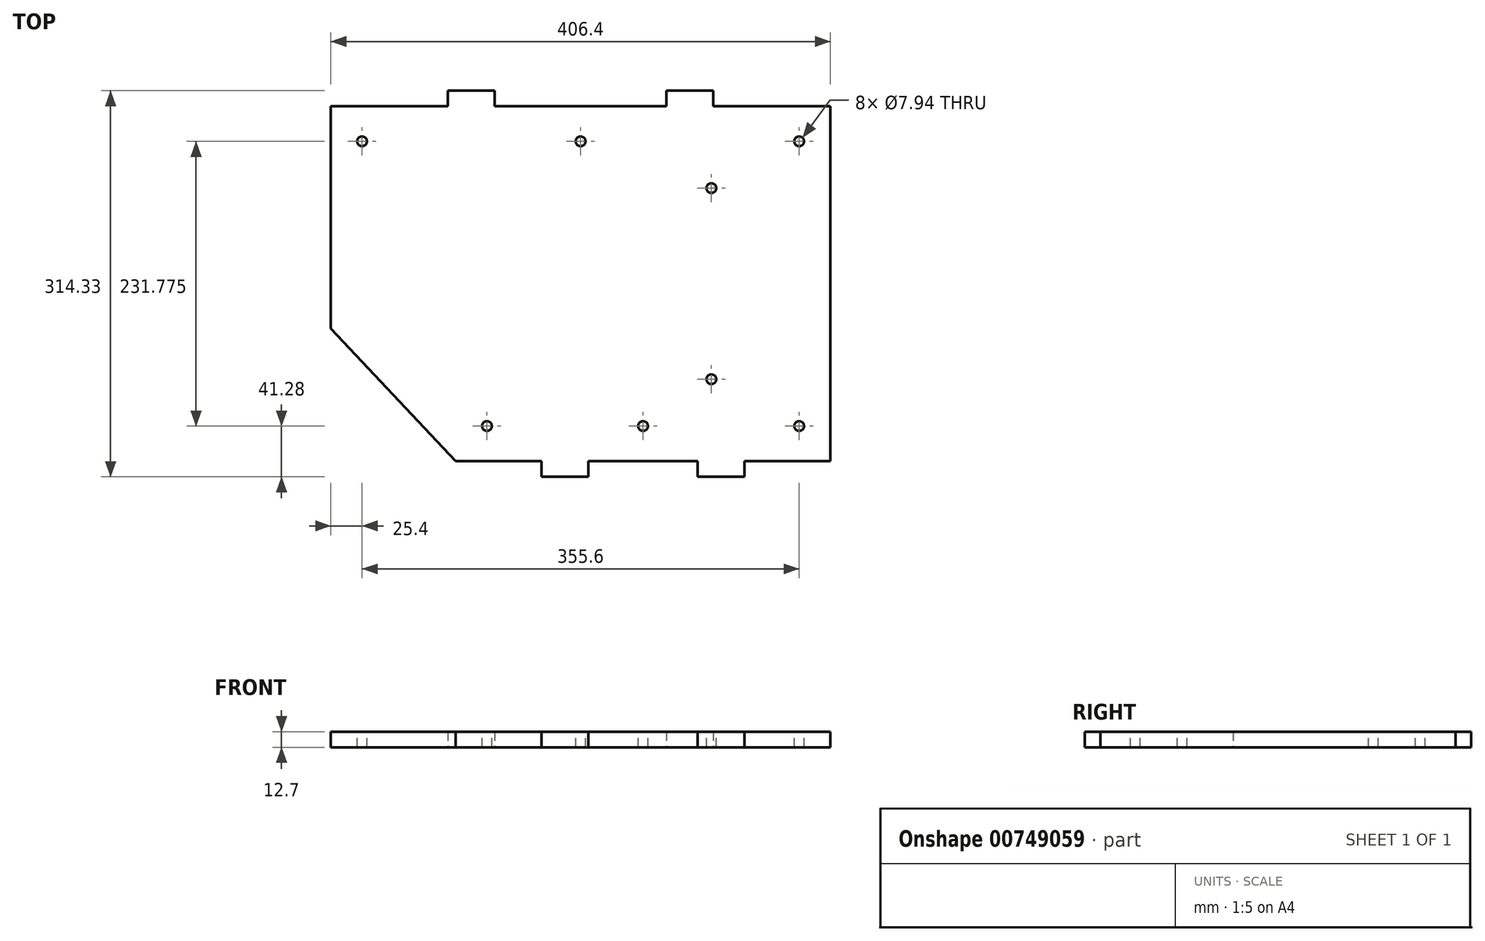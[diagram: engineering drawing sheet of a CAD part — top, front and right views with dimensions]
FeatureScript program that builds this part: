
annotation { "Feature Type Name" : "Feature", "Feature Type Description" : "" }
export const myFeature = defineFeature(function(context is Context, id is Id, definition is map)
    precondition{}
    {
        {
            var Q0;
            Q0=qCreatedBy(makeId("Top.planeOp"),FACE);
            var sketch = newSketch(context, id + "F0", { "sketchPlane" : qUnion([Q0])});
            skLineSegment(sketch, "E0", {"start": v(-127, -25.4) * mm, "end": v(-127, -314.32) * mm});
            skLineSegment(sketch, "E1", {"start": v(-127, -314.32) * mm, "end": v(-196.85, -314.33) * mm});
            skLineSegment(sketch, "E2", {"start": v(-431.8, -314.32) * mm, "end": v(-533.4, -206.38) * mm});
            skLineSegment(sketch, "E3", {"start": v(-533.4, -206.38) * mm, "end": v(-533.4, -25.4) * mm});
            skLineSegment(sketch, "E4", {"start": v(-533.4, -25.4) * mm, "end": v(-438.15, -25.4) * mm});
            skLineSegment(sketch, "E5", {"start": v(-127, -285.75) * mm, "end": v(-458.7, -285.75) * mm, "construction": true});
            skLineSegment(sketch, "E6", {"start": v(-127, -53.98) * mm, "end": v(-533.4, -53.98) * mm, "construction": true});
            skPoint(sketch, "E7", {"position": v(-152.4, -285.75) * mm});
            skPoint(sketch, "E8", {"position": v(-406.4, -285.75) * mm});
            skPoint(sketch, "E9", {"position": v(-279.4, -285.75) * mm});
            skPoint(sketch, "E10", {"position": v(-152.4, -53.98) * mm});
            skPoint(sketch, "E11", {"position": v(-508, -53.98) * mm});
            skPoint(sketch, "E12", {"position": v(-330.2, -53.98) * mm});
            skLineSegment(sketch, "E13", {"start": v(-279.4, -314.33) * mm, "end": v(-279.4, -25.4) * mm, "construction": true});
            skLineSegment(sketch, "E14", {"start": v(-330.2, -25.4) * mm, "end": v(-330.2, -314.33) * mm, "construction": true});
            skLineSegment(sketch, "E15", {"start": v(-215.9, -314.33) * mm, "end": v(-215.9, -263.82) * mm, "construction": true});
            skLineSegment(sketch, "E16", {"start": v(-241.3, -25.4) * mm, "end": v(-241.3, -99.35) * mm, "construction": true});
            skLineSegment(sketch, "E17.top", {"start": v(-234.95, -327.03) * mm, "end": v(-196.85, -327.03) * mm});
            skLineSegment(sketch, "E17.left", {"start": v(-234.95, -314.33) * mm, "end": v(-234.95, -327.02) * mm});
            skLineSegment(sketch, "E17.right", {"start": v(-196.85, -314.32) * mm, "end": v(-196.85, -327.03) * mm});
            skPoint(sketch, "E17.middle", {"position": v(-215.9, -314.33) * mm});
            skLineSegment(sketch, "E18.bottom", {"start": v(-260.35, -12.7) * mm, "end": v(-222.25, -12.7) * mm});
            skLineSegment(sketch, "E18.left", {"start": v(-260.35, -12.7) * mm, "end": v(-260.35, -25.4) * mm});
            skLineSegment(sketch, "E18.right", {"start": v(-222.25, -12.7) * mm, "end": v(-222.25, -25.4) * mm});
            skPoint(sketch, "E18.middle", {"position": v(-241.3, -25.4) * mm});
            skLineSegment(sketch, "E19.MirrorCS", {"start": v(-431.8, -314.33) * mm, "end": v(-361.95, -314.33) * mm});
            skLineSegment(sketch, "E20.MirrorCS", {"start": v(-323.85, -314.33) * mm, "end": v(-323.85, -327.02) * mm});
            skLineSegment(sketch, "E21.MirrorCS", {"start": v(-323.85, -327.03) * mm, "end": v(-361.95, -327.03) * mm});
            skLineSegment(sketch, "E22.MirrorCS", {"start": v(-361.95, -314.33) * mm, "end": v(-361.95, -327.03) * mm});
            skLineSegment(sketch, "E23.MirrorCS", {"start": v(-438.15, -12.7) * mm, "end": v(-438.15, -25.4) * mm});
            skLineSegment(sketch, "E24.MirrorCS", {"start": v(-400.05, -12.7) * mm, "end": v(-400.05, -25.4) * mm});
            skLineSegment(sketch, "E25.MirrorCS", {"start": v(-400.05, -12.7) * mm, "end": v(-438.15, -12.7) * mm});
            skLineSegment(sketch, "E26", {"start": v(-127, -169.86) * mm, "end": v(-434.96, -169.86) * mm, "construction": true});
            skPoint(sketch, "E27", {"position": v(-223.84, -92.08) * mm});
            skPoint(sketch, "E28.MirrorP", {"position": v(-223.84, -247.65) * mm});
            skPoint(sketch, "E29.orphan", {"position": v(-361.95, -301.62) * mm});
            skPoint(sketch, "E30.MirrorCS.start.orphan", {"position": v(-323.85, -301.62) * mm});
            skPoint(sketch, "E31.orphan", {"position": v(-361.95, -301.63) * mm});
            skPoint(sketch, "E32.orphan", {"position": v(-234.95, -301.62) * mm});
            skPoint(sketch, "E33.orphan", {"position": v(-196.85, -301.63) * mm});
            skLineSegment(sketch, "E34.trimOffspring", {"start": v(-400.05, -25.4) * mm, "end": v(-260.35, -25.4) * mm});
            skLineSegment(sketch, "E35.trimOffspring", {"start": v(-222.25, -25.4) * mm, "end": v(-127, -25.4) * mm});
            skLineSegment(sketch, "E36.trimOffspring", {"start": v(-323.85, -314.33) * mm, "end": v(-234.95, -314.33) * mm});
            skLineSegment(sketch, "E37.trimOffspring", {"start": v(-234.95, -314.33) * mm, "end": v(-323.85, -314.33) * mm});
            skLineSegment(sketch, "E38.trimOffspring", {"start": v(-361.95, -314.33) * mm, "end": v(-431.8, -314.33) * mm});
            skLineSegment(sketch, "E39.trimOffspring", {"start": v(-196.85, -314.32) * mm, "end": v(-127, -314.32) * mm});
            skSolve(sketch);
        }
        {
            var Q0;
            Q0 = qSketchRegion(id + "F0", true);
            extrude(context, id + "F1", {"entities" : qUnion([Q0]), "depth" : 12.7 * mm, "offsetDistance" : 25.4 * mm});
        }
        {
            var Q0;
            Q0=sQuery(id+"F0.wireOp",VERTEX,"E8");
            var Q1;
            Q1=sQuery(id+"F0.wireOp",VERTEX,"E28.MirrorP");
            var Q2;
            Q2=sQuery(id+"F0.wireOp",VERTEX,"E7");
            var Q3;
            Q3=sQuery(id+"F0.wireOp",VERTEX,"E9");
            var Q4;
            Q4=sQuery(id+"F0.wireOp",VERTEX,"E27");
            var Q5;
            Q5=sQuery(id+"F0.wireOp",VERTEX,"E10");
            var Q6;
            Q6=sQuery(id+"F0.wireOp",VERTEX,"E12");
            var Q7;
            Q7=sQuery(id+"F0.wireOp",VERTEX,"E11");
            var Q8;
            Q8=makeQuery(id+"F1.opExtrude","SWEPT_BODY",BODY,{"disambiguationData":[OSD([sQuery(id+"F0.wireOp",EDGE,"E0"),sQuery(id+"F0.wireOp",EDGE,"E2"),sQuery(id+"F0.wireOp",EDGE,"E3"),sQuery(id+"F0.wireOp",EDGE,"E4"),sQuery(id+"F0.wireOp",EDGE,"E17.top"),sQuery(id+"F0.wireOp",EDGE,"E17.left"),sQuery(id+"F0.wireOp",EDGE,"E17.right"),sQuery(id+"F0.wireOp",EDGE,"E18.bottom"),sQuery(id+"F0.wireOp",EDGE,"E18.left"),sQuery(id+"F0.wireOp",EDGE,"E18.right"),sQuery(id+"F0.wireOp",EDGE,"E19.MirrorCS"),sQuery(id+"F0.wireOp",EDGE,"E20.MirrorCS"),sQuery(id+"F0.wireOp",EDGE,"E21.MirrorCS"),sQuery(id+"F0.wireOp",EDGE,"E22.MirrorCS"),sQuery(id+"F0.wireOp",EDGE,"E23.MirrorCS"),sQuery(id+"F0.wireOp",EDGE,"E24.MirrorCS"),sQuery(id+"F0.wireOp",EDGE,"E25.MirrorCS")])]});
            hole(context, id + "F2", {"style" : HoleStyle.SIMPLE, "endStyle" : HoleEndStyle.BLIND, "oppositeDirection" : true, "standardTappedOrClearance" : lookupTablePath({ "standard" : "ANSI", "engagement" : "75%", "pitch" : "16 tpi", "size" : "3/8", "type" : "Tapped" }), "standardBlindInLast" : lookupTablePath({ "standard" : "ANSI", "engagement" : "75%", "pitch" : "16 tpi", "size" : "3/8", "type" : "Tapped" }), "holeDiameter" : 7.94 * mm, "majorDiameter" : 9.52 * mm, "showTappedDepth" : true, "holeDepth" : 17.48 * mm, "isTappedThrough" : true, "tappedDepth" : 12.71 * mm, "tapClearance" : 3, "locations" : qUnion([Q0, Q1, Q2, Q3, Q4, Q5, Q6, Q7]), "scope" : qUnion([Q8])});
        }
    });
